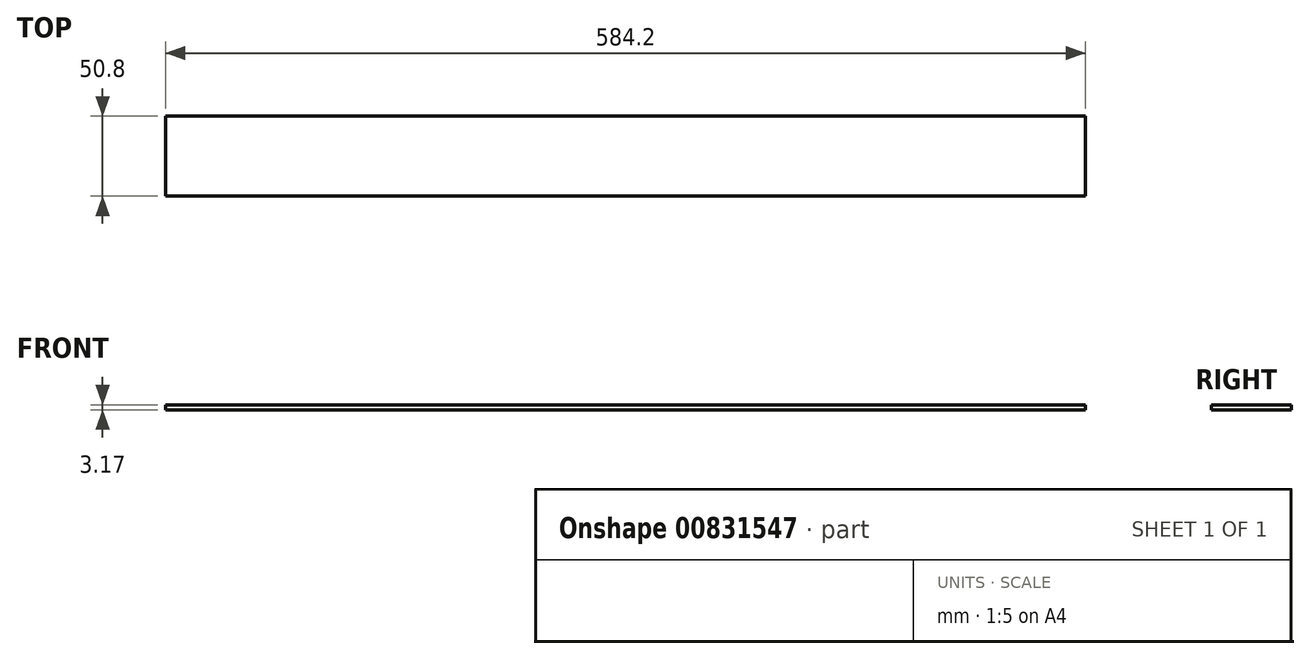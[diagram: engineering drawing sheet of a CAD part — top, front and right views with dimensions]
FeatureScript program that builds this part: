
annotation { "Feature Type Name" : "Feature", "Feature Type Description" : "" }
export const myFeature = defineFeature(function(context is Context, id is Id, definition is map)
    precondition{}
    {
        {
            var Q0;
            Q0=qCreatedBy(makeId("Top.planeOp"),FACE);
            var sketch = newSketch(context, id + "F0", { "sketchPlane" : qUnion([Q0])});
            skLineSegment(sketch, "E0.bottom", {"start": v(0, 0) * mm, "end": v(584.2, 0) * mm});
            skLineSegment(sketch, "E0.top", {"start": v(0, 50.8) * mm, "end": v(584.2, 50.8) * mm});
            skLineSegment(sketch, "E0.left", {"start": v(0, 0) * mm, "end": v(0, 50.8) * mm});
            skLineSegment(sketch, "E0.right", {"start": v(584.2, 0) * mm, "end": v(584.2, 50.8) * mm});
            skSolve(sketch);
        }
        {
            var Q0;
            Q0=makeQuery(id+"F0.imprint","IMPRINT",FACE,{"disambiguationData":[TD([[makeQuery(id+"F0.imprint","IMPRINT",EDGE,{"derivedFrom":sQuery(id+"F0.wireOp",EDGE,"E0.bottom")}),1.0]])]});
            extrude(context, id + "F1", {"entities" : qUnion([Q0]), "depth" : 3.17 * mm, "offsetDistance" : 25.4 * mm});
        }
    });
